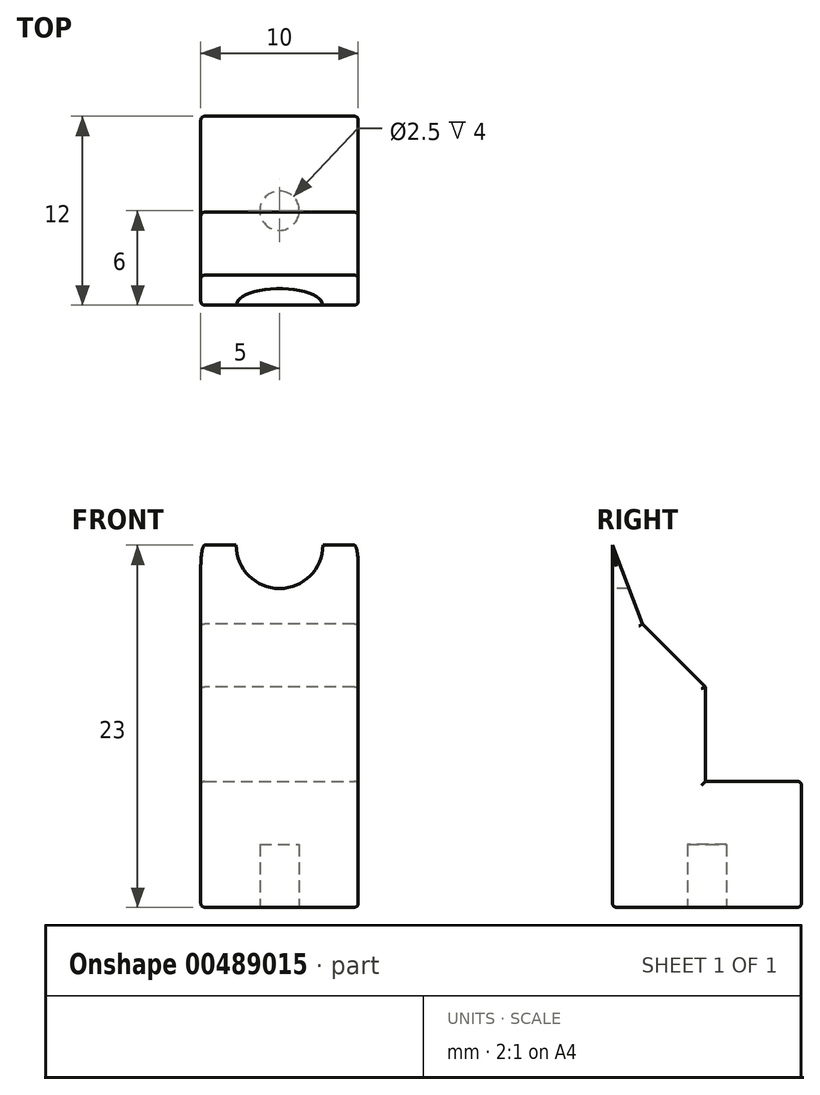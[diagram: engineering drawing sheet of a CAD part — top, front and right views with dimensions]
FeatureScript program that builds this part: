
annotation { "Feature Type Name" : "Feature", "Feature Type Description" : "" }
export const myFeature = defineFeature(function(context is Context, id is Id, definition is map)
    precondition{}
    {
        {
            var Q0;
            Q0=qCreatedBy(makeId("Top.planeOp"),FACE);
            var sketch = newSketch(context, id + "F0", { "sketchPlane" : qUnion([Q0])});
            skLineSegment(sketch, "E0.bottom", {"start": v(0, 0) * mm, "end": v(10, 0) * mm});
            skLineSegment(sketch, "E0.top", {"start": v(0, 12) * mm, "end": v(10, 12) * mm});
            skLineSegment(sketch, "E0.left", {"start": v(0, 0) * mm, "end": v(0, 12) * mm});
            skLineSegment(sketch, "E0.right", {"start": v(10, 0) * mm, "end": v(10, 12) * mm});
            skSolve(sketch);
        }
        {
            var Q0;
            Q0=makeQuery(id+"F0.imprint","IMPRINT",FACE,{"disambiguationData":[TD([[makeQuery(id+"F0.imprint","IMPRINT",EDGE,{"derivedFrom":sQuery(id+"F0.wireOp",EDGE,"E0.bottom")}),1.0]])]});
            extrude(context, id + "F1", {"entities" : qUnion([Q0]), "depth" : 8 * mm});
        }
        {
            var Q0;
            Q0=makeQuery(id+"F1.opExtrude","CAP_FACE",FACE,{"disambiguationData":[OSD([sQuery(id+"F0.wireOp",EDGE,"E0.bottom"),sQuery(id+"F0.wireOp",EDGE,"E0.top"),sQuery(id+"F0.wireOp",EDGE,"E0.left"),sQuery(id+"F0.wireOp",EDGE,"E0.right")])],"isStart":false});
            var sketch = newSketch(context, id + "F2", { "sketchPlane" : qUnion([Q0])});
            skLineSegment(sketch, "E1.bottom", {"start": v(0, 0) * mm, "end": v(10, 0) * mm});
            skLineSegment(sketch, "E1.top", {"start": v(0, 5.9) * mm, "end": v(10, 5.9) * mm});
            skLineSegment(sketch, "E1.left", {"start": v(0, 0) * mm, "end": v(0, 5.9) * mm});
            skLineSegment(sketch, "E1.right", {"start": v(10, 0) * mm, "end": v(10, 5.9) * mm});
            skSolve(sketch);
        }
        {
            var Q0;
            Q0=makeQuery(id+"F2.imprint","IMPRINT",FACE,{"disambiguationData":[TD([[makeQuery(id+"F2.imprint","IMPRINT",EDGE,{"derivedFrom":sQuery(id+"F2.wireOp",EDGE,"E1.bottom")}),1.0]])]});
            extrude(context, id + "F3", {"entities" : qUnion([Q0]), "operationType" : NewBodyOperationType.ADD, "depth" : 15 * mm});
        }
        {
            var Q0;
            Q0=makeQuery(id+"F3.boolean.opBoolean","MERGE",FACE,{"derivedFrom":[makeQuery(id+"F1.opExtrude","SWEPT_FACE",FACE,{"disambiguationData":[OSD([sQuery(id+"F0.wireOp",EDGE,"E0.left")])]}),makeQuery(id+"F3.opExtrude","SWEPT_FACE",FACE,{"disambiguationData":[OSD([sQuery(id+"F2.wireOp",EDGE,"E1.left")])]})]});
            var sketch = newSketch(context, id + "F4", { "sketchPlane" : qUnion([Q0])});
            skLineSegment(sketch, "E2.bottom", {"start": v(-5.9, 18) * mm, "end": v(-1.9, 18) * mm});
            skLineSegment(sketch, "E2.top", {"start": v(-5.9, 23) * mm, "end": v(-1.9, 23) * mm});
            skLineSegment(sketch, "E2.left", {"start": v(-5.9, 18) * mm, "end": v(-5.9, 23) * mm});
            skLineSegment(sketch, "E2.right", {"start": v(-1.9, 18) * mm, "end": v(-1.9, 23) * mm});
            skLineSegment(sketch, "E3", {"start": v(-1.9, 18) * mm, "end": v(-5.9, 14) * mm});
            skLineSegment(sketch, "E4", {"start": v(-5.9, 14) * mm, "end": v(-5.9, 18) * mm});
            skLineSegment(sketch, "E5", {"start": v(-1.9, 18) * mm, "end": v(0, 23) * mm});
            skLineSegment(sketch, "E6", {"start": v(-1.9, 23) * mm, "end": v(0, 23) * mm});
            skSolve(sketch);
        }
        {
            var Q0;
            Q0=makeQuery(id+"F4.imprint","IMPRINT",FACE,{"disambiguationData":[TD([[makeQuery(id+"F4.imprint","IMPRINT",EDGE,{"derivedFrom":sQuery(id+"F4.wireOp",EDGE,"E2.bottom")}),-1.0]])]});
            var Q1;
            Q1=makeQuery(id+"F4.imprint","IMPRINT",FACE,{"disambiguationData":[TD([[makeQuery(id+"F4.imprint","IMPRINT",EDGE,{"derivedFrom":sQuery(id+"F4.wireOp",EDGE,"E2.bottom")}),1.0]])]});
            var Q2;
            Q2=makeQuery(id+"F4.imprint","IMPRINT",FACE,{"disambiguationData":[TD([[makeQuery(id+"F4.imprint","IMPRINT",EDGE,{"derivedFrom":sQuery(id+"F4.wireOp",EDGE,"E2.right")}),-1.0]])]});
            var Q3;
            Q3=makeQuery(id+"F3.boolean.opBoolean","MERGE",FACE,{"derivedFrom":[makeQuery(id+"F1.opExtrude","SWEPT_FACE",FACE,{"disambiguationData":[OSD([sQuery(id+"F0.wireOp",EDGE,"E0.right")])]}),makeQuery(id+"F3.opExtrude","SWEPT_FACE",FACE,{"disambiguationData":[OSD([sQuery(id+"F2.wireOp",EDGE,"E1.right")])]})]});
            extrude(context, id + "F5", {"entities" : qUnion([Q0, Q1, Q2]), "operationType" : NewBodyOperationType.REMOVE, "endBound" : BoundingType.UP_TO_SURFACE, "oppositeDirection" : true, "endBoundEntityFace" : qUnion([Q3]), "depth" : 25 * mm});
        }
        {
            var Q0;
            Q0=makeQuery(id+"F3.boolean.opBoolean","MERGE",FACE,{"derivedFrom":[makeQuery(id+"F1.opExtrude","SWEPT_FACE",FACE,{"disambiguationData":[OSD([sQuery(id+"F0.wireOp",EDGE,"E0.bottom")])]}),makeQuery(id+"F3.opExtrude","SWEPT_FACE",FACE,{"disambiguationData":[OSD([sQuery(id+"F2.wireOp",EDGE,"E1.bottom")])]})]});
            var sketch = newSketch(context, id + "F6", { "sketchPlane" : qUnion([Q0])});
            skCircle(sketch, "E7", {"center": v(5, 23) * mm, "radius": 2.75 * mm});
            skSolve(sketch);
        }
        {
            var Q0;
            {var subQ0=sQuery(id+"F6.wireOp",EDGE,"E7");var subQ1=sQuery(id+"F2.wireOp",EDGE,"E1.bottom");var subQ2=makeQuery(id+"F5.boolean.opBoolean","MERGE",EDGE,{"derivedFrom":[makeQuery(id+"F3.opExtrude","CAP_EDGE",EDGE,{"disambiguationData":[OSD([subQ1])],"isStart":false}),makeQuery(id+"F5.opExtrude","SWEPT_EDGE",EDGE,{"disambiguationData":[OSD([sQuery(id+"F0.wireOp",EDGE,"E0.bottom"),sQuery(id+"F0.wireOp",EDGE,"E0.left"),subQ1,sQuery(id+"F2.wireOp",EDGE,"E1.left"),sQuery(id+"F4.wireOp",EDGE,"E5"),sQuery(id+"F4.wireOp",EDGE,"E6")])]})]});var subQ3=makeQuery(id+"F6.imprint","INTERSECT",VERTEX,{"disambiguationData":[OD(0.0)],"derivedFrom":[subQ2,subQ0]});Q0=makeQuery(id+"F6.imprint","IMPRINT",FACE,{"disambiguationData":[TD([[makeQuery(id+"F6.imprint","IMPRINT",EDGE,{"disambiguationData":[TD([[subQ3,-1.0]])],"derivedFrom":subQ0}),1.0]])]});}
            extrude(context, id + "F7", {"entities" : qUnion([Q0]), "operationType" : NewBodyOperationType.REMOVE, "oppositeDirection" : true, "depth" : 25 * mm});
        }
        {
            var Q0;
            Q0=makeQuery(id+"F3.boolean.opBoolean","MERGE",FACE,{"derivedFrom":[makeQuery(id+"F1.opExtrude","SWEPT_FACE",FACE,{"disambiguationData":[OSD([sQuery(id+"F0.wireOp",EDGE,"E0.right")])]}),makeQuery(id+"F3.opExtrude","SWEPT_FACE",FACE,{"disambiguationData":[OSD([sQuery(id+"F2.wireOp",EDGE,"E1.right")])]})]});
            var Q1;
            Q1=makeQuery(id+"F3.boolean.opBoolean","MERGE",FACE,{"derivedFrom":[makeQuery(id+"F1.opExtrude","SWEPT_FACE",FACE,{"disambiguationData":[OSD([sQuery(id+"F0.wireOp",EDGE,"E0.left")])]}),makeQuery(id+"F3.opExtrude","SWEPT_FACE",FACE,{"disambiguationData":[OSD([sQuery(id+"F2.wireOp",EDGE,"E1.left")])]})]});
            var Q2;
            Q2=makeQuery(id+"F1.opExtrude","SWEPT_FACE",FACE,{"disambiguationData":[OSD([sQuery(id+"F0.wireOp",EDGE,"E0.top")])]});
            var Q3;
            Q3=makeQuery(id+"F1.opExtrude","CAP_EDGE",EDGE,{"disambiguationData":[OSD([sQuery(id+"F0.wireOp",EDGE,"E0.bottom")])],"isStart":true});
            fillet(context, id + "F8", {"entities" : qUnion([Q0, Q1, Q2, Q3]), "radius" : 0.25 * mm, "tangentPropagation" : true, "allowEdgeOverflow" : false});
        }
        {
            var Q0;
            Q0=makeQuery(id+"F1.opExtrude","CAP_FACE",FACE,{"disambiguationData":[OSD([sQuery(id+"F0.wireOp",EDGE,"E0.bottom"),sQuery(id+"F0.wireOp",EDGE,"E0.top"),sQuery(id+"F0.wireOp",EDGE,"E0.left"),sQuery(id+"F0.wireOp",EDGE,"E0.right")])],"isStart":true});
            var sketch = newSketch(context, id + "F9", { "sketchPlane" : qUnion([Q0])});
            skLineSegment(sketch, "E8", {"start": v(5, -0.25) * mm, "end": v(5, -11.75) * mm, "construction": true});
            skCircle(sketch, "E9", {"center": v(5, -6) * mm, "radius": 1.25 * mm});
            skSolve(sketch);
        }
        {
            var Q0;
            Q0 = qSketchRegion(id + "F9", true);
            extrude(context, id + "F10", {"entities" : qUnion([Q0]), "operationType" : NewBodyOperationType.REMOVE, "oppositeDirection" : true, "depth" : 4 * mm});
        }
    });
